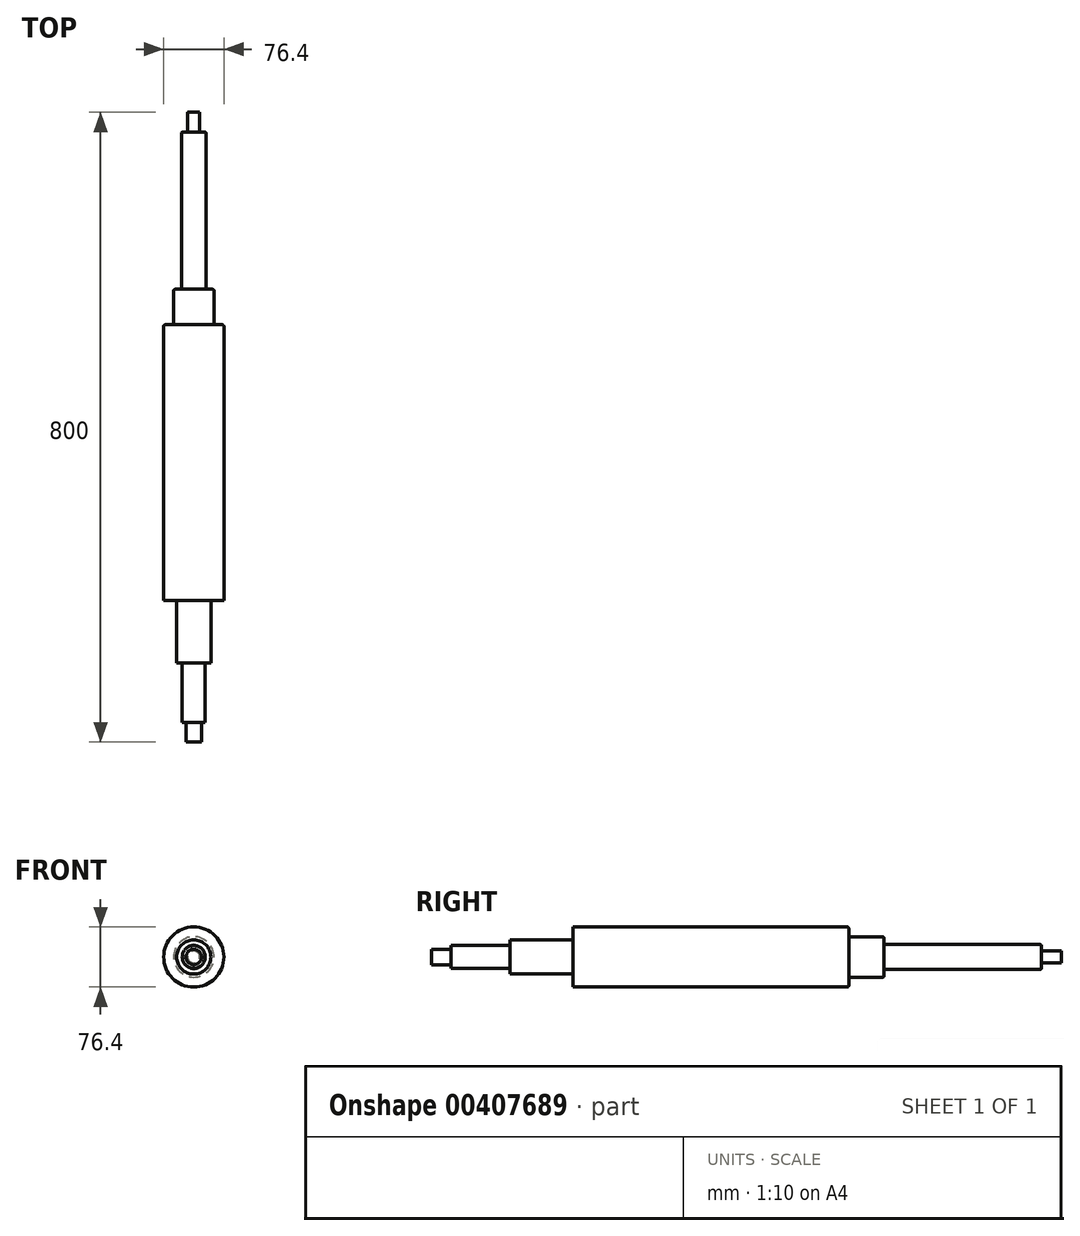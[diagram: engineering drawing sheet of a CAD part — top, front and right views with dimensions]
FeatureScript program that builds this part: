
annotation { "Feature Type Name" : "Feature", "Feature Type Description" : "" }
export const myFeature = defineFeature(function(context is Context, id is Id, definition is map)
    precondition{}
    {
        {
            var Q0;
            Q0=qCreatedBy(makeId("Front.planeOp"),FACE);
            var sketch = newSketch(context, id + "F0", { "sketchPlane" : qUnion([Q0])});
            skCircle(sketch, "E0", {"center": v(0, 0) * mm, "radius": 38.2 * mm});
            skSolve(sketch);
        }
        {
            var Q0;
            Q0 = qSketchRegion(id + "F0", true);
            extrude(context, id + "F1", {"entities" : qUnion([Q0]), "depth" : 350 * mm});
        }
        {
            var Q0;
            Q0=makeQuery(id+"F1.opExtrude","CAP_FACE",FACE,{"disambiguationData":[OSD([sQuery(id+"F0.wireOp",EDGE,"E0")])],"isStart":true});
            var sketch = newSketch(context, id + "F2", { "sketchPlane" : qUnion([Q0])});
            skCircle(sketch, "E1", {"center": v(0, 0) * mm, "radius": 25.72 * mm});
            skSolve(sketch);
        }
        {
            var Q0;
            Q0 = qSketchRegion(id + "F2", true);
            extrude(context, id + "F3", {"entities" : qUnion([Q0]), "operationType" : NewBodyOperationType.ADD, "depth" : 45 * mm});
        }
        {
            var Q0;
            Q0=makeQuery(id+"F3.opExtrude","CAP_FACE",FACE,{"disambiguationData":[OSD([sQuery(id+"F2.wireOp",EDGE,"E1")])],"isStart":false});
            var sketch = newSketch(context, id + "F4", { "sketchPlane" : qUnion([Q0])});
            skCircle(sketch, "E2", {"center": v(0, 0) * mm, "radius": 15.73 * mm});
            skSolve(sketch);
        }
        {
            var Q0;
            Q0=makeQuery(id+"F4.imprint","IMPRINT",FACE,{"disambiguationData":[TD([[makeQuery(id+"F4.imprint","IMPRINT",EDGE,{"derivedFrom":sQuery(id+"F4.wireOp",EDGE,"E2")}),1.0]])]});
            extrude(context, id + "F5", {"entities" : qUnion([Q0]), "operationType" : NewBodyOperationType.ADD, "depth" : 200 * mm});
        }
        {
            var Q0;
            Q0=makeQuery(id+"F5.opExtrude","CAP_EDGE",EDGE,{"disambiguationData":[OSD([sQuery(id+"F4.wireOp",EDGE,"E2")])],"isStart":false});
            var Q1;
            Q1=makeQuery(id+"F3.opExtrude","CAP_EDGE",EDGE,{"disambiguationData":[OSD([sQuery(id+"F2.wireOp",EDGE,"E1")])],"isStart":false});
            var Q2;
            Q2=makeQuery(id+"F1.opExtrude","CAP_EDGE",EDGE,{"disambiguationData":[OSD([sQuery(id+"F0.wireOp",EDGE,"E0")])],"isStart":true});
            fillet(context, id + "F6", {"entities" : qUnion([Q0, Q1, Q2]), "radius" : 2 * mm, "tangentPropagation" : true, "allowEdgeOverflow" : false});
        }
        {
            var Q0;
            Q0=makeQuery(id+"F5.opExtrude","CAP_FACE",FACE,{"disambiguationData":[OSD([sQuery(id+"F4.wireOp",EDGE,"E2")])],"isStart":false});
            var sketch = newSketch(context, id + "F7", { "sketchPlane" : qUnion([Q0])});
            skCircle(sketch, "E3", {"center": v(0, 0) * mm, "radius": 7.72 * mm});
            skSolve(sketch);
        }
        {
            var Q0;
            Q0=makeQuery(id+"F7.imprint","IMPRINT",FACE,{"disambiguationData":[TD([[makeQuery(id+"F7.imprint","IMPRINT",EDGE,{"derivedFrom":sQuery(id+"F7.wireOp",EDGE,"E3")}),1.0]])]});
            extrude(context, id + "F8", {"entities" : qUnion([Q0]), "operationType" : NewBodyOperationType.ADD, "depth" : 25 * mm});
        }
        {
            var Q0;
            Q0=makeQuery(id+"F1.opExtrude","CAP_FACE",FACE,{"disambiguationData":[OSD([sQuery(id+"F0.wireOp",EDGE,"E0")])],"isStart":false});
            var sketch = newSketch(context, id + "F9", { "sketchPlane" : qUnion([Q0])});
            skCircle(sketch, "E4", {"center": v(0, 0) * mm, "radius": 21.7 * mm});
            skSolve(sketch);
        }
        {
            var Q0;
            Q0 = qSketchRegion(id + "F9", true);
            extrude(context, id + "F10", {"entities" : qUnion([Q0]), "operationType" : NewBodyOperationType.ADD, "depth" : 80 * mm});
        }
        {
            var Q0;
            Q0=makeQuery(id+"F10.opExtrude","CAP_FACE",FACE,{"disambiguationData":[OSD([sQuery(id+"F9.wireOp",EDGE,"E4")])],"isStart":false});
            var sketch = newSketch(context, id + "F11", { "sketchPlane" : qUnion([Q0])});
            skCircle(sketch, "E5", {"center": v(0, 0) * mm, "radius": 14.57 * mm});
            skSolve(sketch);
        }
        {
            var Q0;
            Q0 = qSketchRegion(id + "F11", true);
            extrude(context, id + "F12", {"entities" : qUnion([Q0]), "operationType" : NewBodyOperationType.ADD, "depth" : 75 * mm});
        }
        {
            var Q0;
            Q0=makeQuery(id+"F12.opExtrude","CAP_FACE",FACE,{"disambiguationData":[OSD([sQuery(id+"F11.wireOp",EDGE,"E5")])],"isStart":false});
            var sketch = newSketch(context, id + "F13", { "sketchPlane" : qUnion([Q0])});
            skCircle(sketch, "E6", {"center": v(0, 0) * mm, "radius": 9.83 * mm});
            skSolve(sketch);
        }
        {
            var Q0;
            Q0=makeQuery(id+"F13.imprint","IMPRINT",FACE,{"disambiguationData":[TD([[makeQuery(id+"F13.imprint","IMPRINT",EDGE,{"derivedFrom":sQuery(id+"F13.wireOp",EDGE,"E6")}),1.0]])]});
            extrude(context, id + "F14", {"entities" : qUnion([Q0]), "operationType" : NewBodyOperationType.ADD, "depth" : 25 * mm});
        }
    });
